# Revit family: Mixer tap-Wall_mounted-PRESTO-MURAL NEO CHAUD 65MM 7SEC-66105
name_source: partatom
category: Plumbing Fixtures
revit_build: Autodesk Revit Architecture 2014 (Build: 20130308_1515(x64)
units: mm (PartAtom-declared; Revit-internal decimal feet)

## types (1)
- 66105
    Description = PRESTO NEO Robinet simple temporisé mural (65mm)
    Durée = 7.0 s
    Durée (réglage à 4 positions) = 7 secondes (± 5 sec.)
    Débit (à 3 bar - régulateur de débit à 4 positions) = 3 l/min à 3 bar
    Edition number = 1
    Entrée EC = 13 mm
    Entrée EF = 0 mm  [stored 0 ft]
    Garantie = 10
    HW Connection = Yes
    Hauteur = 0 mm  [stored 0 ft]
    Largeur = 104 mm
    Lenght = 0 mm  [stored 0 ft]
    Manufacturer = PRESTO LES ROBINETS
    Manufacturer name = Presto
    Material main = Stainless steel
    Material secondary = Stainless steel
    Matériau Principal = Acier inoxydable
    Model = 66105
    Nominal height = 10400
    Nominal width = 0
    Pression de fonctionnement = 1 à 5 bar
    Product Guid = 014f790e-aa24-462e-a9f3-6ca5964c11a0
    Product SKU = 66030
    Product data url = http://bimobject.com
    Product family = NEO
    Product group = ROBINET
    QR code = http://bimobject.com
    Temp - Résistance (Choc Thermique de 30 Minutes) = 75 °C
    Weight Net (Kg) = 0

note: [stored X ft] marks values corroborated as IEEE doubles in the binary element streams (Revit-internal decimal feet)

## geometry (parser evidence)
native form markers: Blend x2, Sweep x16
no freeform markers — native parametric forms only
